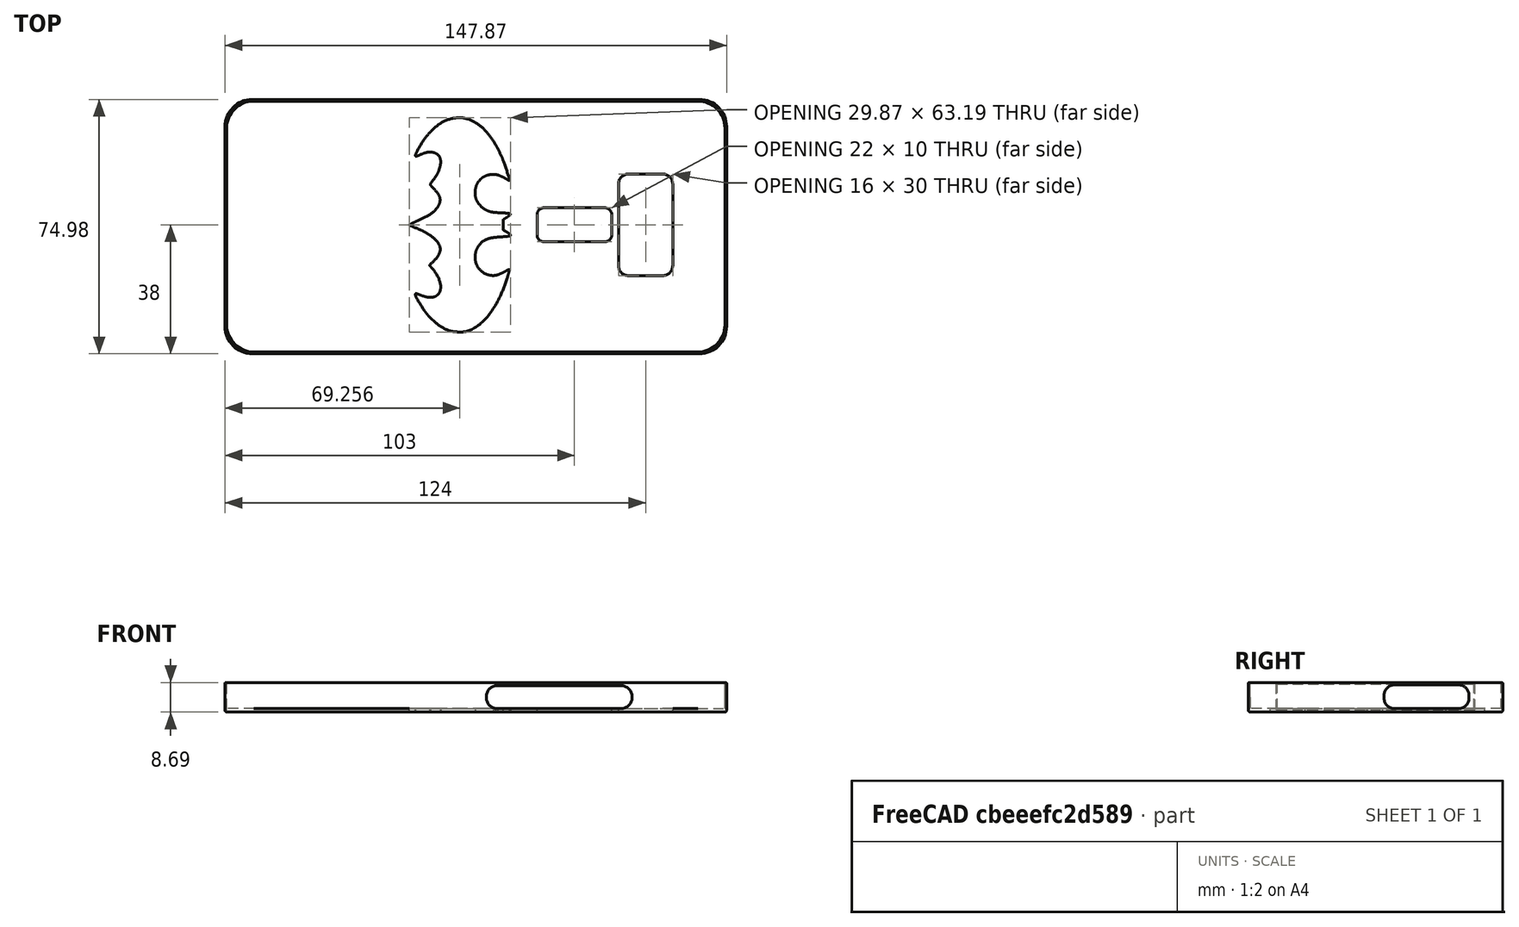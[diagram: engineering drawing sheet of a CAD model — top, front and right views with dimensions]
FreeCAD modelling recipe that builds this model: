
FCSTD DOCUMENT  (FreeCAD 0.16R6706 (Git))
Label: cover_zenphone3
License: All rights reserved
LicenseURL: http://en.wikipedia.org/wiki/All_rights_reserved
objects: Part::Fillet×9, Part::Box×7, Part::Cut×7, Part::Feature×2, Part::Extrusion×2, Part::MultiFuse×1, Part::FeaturePython×1
note: 29 computed .brp shape members not serialized (recipe doc carries the construction recipe); baked Part::Feature solids carry a one-line shape summary decoded from their .brp

FEATURE [Part::Box] Box  label="Cubo"
  Height = 8.69
  Length = 147.87
  Width = 74.98
FEATURE [Part::Box] Box001  label="Cubo001"
  Height = 7.69
  Length = 146.87
  Placement = pos=(0.5,0.5,1) rot=(0,0,1;0rad)
  Width = 73.98
FEATURE [Part::Cut] Cut
  Base = -> Box
  Tool = -> Box001
FEATURE [Part::Fillet] Fillet
  Base = -> Cut
  Edges = 8 edges r=8: [Edge1,Edge3,Edge6,Edge15,Edge18,Edge19,Edge20,Edge23]
FEATURE [Part::Box] Box002  label="Cubo002"
  Height = 1
  Length = 16
  Placement = pos=(116,23,0) rot=(0,0,1;0rad)
  Width = 30
FEATURE [Part::Cut] Cut001
  Base = -> Fillet
  Tool = -> Box002
FEATURE [Part::Fillet] Fillet001
  Base = -> Cut001
  Edges = 4 edges r=3: [Edge53,Edge55,Edge56,Edge58]
FEATURE [Part::Box] Box003  label="Cubo003"
  Height = 1
  Length = 22
  Placement = pos=(92,33,0) rot=(0,0,1;0rad)
  Width = 10
FEATURE [Part::Cut] Cut002
  Base = -> Fillet001
  Tool = -> Box003
FEATURE [Part::Fillet] Fillet002
  Base = -> Cut002
  Edges = 4 edges r=2: [Edge37,Edge39,Edge40,Edge42]
FEATURE [Part::Box] Box004  label="Cubo004"
  Height = 7.69
  Length = 0.5
  Placement = pos=(0,8.3,0.6) rot=(0,0,1;0rad)
  Width = 58.44
FEATURE [Part::Cut] Cut003
  Base = -> Fillet002
  Tool = -> Box004
FEATURE [Part::Fillet] Fillet003
  Base = -> Cut003
  Edges = 4 edges r=0.1: [Edge93,Edge95,Edge96,Edge99]
FEATURE [Part::Box] Box005  label="Cubo005"
  Height = 6.79
  Length = 43
  Placement = pos=(77,0,1) rot=(0,0,1;0rad)
  Width = 0.5
FEATURE [Part::Cut] Cut004
  Base = -> Fillet003
  Tool = -> Box005
FEATURE [Part::Fillet] Fillet004
  Base = -> Cut004
  Edges = 4 edges r=3.3: [Edge134,Edge135,Edge136,Edge137]
FEATURE [Part::Fillet] Fillet005
  Base = -> Fillet004
  Edges = 1 edges r=0.5: [Edge9]
FEATURE [Part::Fillet] Fillet006
  Base = -> Fillet005
  Edges = 1 edges r=0.2: [Edge25]
FEATURE [Part::Fillet] Fillet007
  Base = -> Fillet006
  Edges = 1 edges r=0.2: [Edge12]
FEATURE [Part::Box] Box006  label="Cubo006"
  Height = 7
  Length = 0.5
  Placement = pos=(147.37,40,1) rot=(0,0,1;0rad)
  Width = 25
FEATURE [Part::Cut] Cut005
  Base = -> Fillet007
  Tool = -> Box006
FEATURE [Part::Fillet] Fillet008
  Base = -> Cut005
  Edges = 4 edges r=3: [Edge154,Edge155,Edge157,Edge158]
FEATURE [Part::Feature] Path
  shape: bbox 351.7 x 166.1 x 2e-07 mm, 0 faces, 0 solids (baked)
FEATURE [Part::Feature] Path001
  shape: bbox 351.7 x 166.1 x 2e-07 mm, 0 faces, 0 solids (baked)
FEATURE [Part::Extrusion] Extrude
  Base = -> Path001
  Dir = (0,0,1)
  Solid = true
FEATURE [Part::Extrusion] Extrude001
  Base = -> Path001
  Dir = (0,0,1)
  Solid = true
FEATURE [Part::MultiFuse] Fusion
  Shapes = -> [Extrude001,Extrude]
FEATURE [Part::FeaturePython] Scale  # Draft clone (typed FeaturePython)
  Objects = -> [Fusion]
  Placement = pos=(40,70.5,0) rot=(0,0,-1;1.5708rad)
  Scale = (0.18,0.18,1)
FEATURE [Part::Cut] Cut006
  Base = -> Fillet008
  Tool = -> Scale
